# Revit family: HD148-2016.10.03-BT-STRIPSCREEN
name_source: partatom
category: Modelos genéricos
revit_build: Autodesk Revit 2017 (Build: 20160225_1515(x64)
units: mm (PartAtom-declared; Revit-internal decimal feet)

## family parameters
Compartido = No
Corte con vacíos al cargar = No
Cota de conector redondo = Diámetro de uso
Puede alojar armadura = No
Punto de cálculo de habitación = No
Se basa en plano de trabajo = No
Siempre vertical = Sí
Tipo de pieza = Normal

## types (1)
- Productos HD
    Alto THB = 1700 mm
    Ancho = 380 mm  [stored 1.24672 ft]
    BT_Alto = Aluzinc:12 mts, Acero corten: 15 mts
    BT_Ancho = 605 mm
    BT_Codigo_Origen = HD0148
    BT_Color = 100 colores a eleccion
    BT_Código_Línea = De Linea
    BT_Descripcion = Fleje de geometría plana Stripscreen con un ancho de 500mm y un largo
máximo de 5000 mm
    BT_EETT = Fleje de geometría plana con un ancho de 500mm y un largo
máximo de 5000 mm, fabricado en Aluzinc de espesor 1 mm.
El esquema de pintura considera la aplicación de un primer poliéster
de secado al horno por ambas caras, con un espesor de 5 ± 2
micras, y la aplicación de un esmalte de terminación poliéster
secado al horno por ambas caras, con un espesor total de 25 ± 2
micras (incluido el primer).
El sistema de instalación considera en su extremo inferior resortes
de acero inoxidable según cálculo y en su extremo superior
considera tensores de fierro galvanizado que permiten tensar el
fleje, los cuales se unen a éste mediante grilletes galvanizados
cuyas dimensiones se definirán de acuerdo a los requerimientos del
proyecto. Para evitar la ruptura del material en el tiempo, el fleje se
dobla en ambos extremos por sobre una barra de aluminio de 10
mm de diámetro y luego se prensa con 2 pletinas de aluminio de 50
mm de altura y 3mm de espesor que se fijarán mediante pernos y
tuercas.

que presentan una geometría transversal circular, con un diámetro de 

41 mm, los que son fabricados en aluzinc de espesor 0,5 mm.

El avance del panel es de 51 mm a eje.

El esquema de pintura considera la aplicación de un primer poliéster 

de secado al horno por ambas caras, con un espesor de 5 ±  2 micras, 

en color verde o gris y la aplicación de un esmalte de terminación 

poliéster secado al horno por una cara, con un espesor total de 25 ±  2 

micras (incluido el primer)

Se considera el uso de un perfil mullion ranurado, el que es fabricado 

en aluzinc de espesor 1,5 mm junto a otros accesorios propios de la 

solución definida, como la escuadra y traba.

Opciones de perforado estándar: #103 - Microperforados
    BT_Elemento = Celosías y Quiebravistas
    BT_Especialidad = Arquitectura
    BT_Fabricante = Hunter Douglas
    BT_Itemizado_Estandar_CDT = D 01 08 80
    BT_Marca = Hunter Douglas
    BT_MasterFormat® = 08 91 19
    BT_Material = Aluzinc 0.6-0.8-1.0mm, Acero corten: 0.6-1.0 mm
    BT_Nombre_Corto = Stripscreen
    BT_Nombre_Tecnico = Stripscreen
    BT_Peso = Aluzinc: 4.8-6.3-7.9 Kg/m2, Acero corten: 4.8-7.9 Kg/m2
    BT_Profundidad = Largo Máximo Aluzinc: 12 mts, Largo máximo Acero corten: 15 mts
    BT_SKU = 00 31 66
    BT_Uso = Exterior
    BT_Web_del_Producto = http://www.hunterdouglas.cl
    ID_Objeto = BT_F_F_770
    ID_Source = BIMTOOL
    Material = Metal

note: [stored X ft] marks values corroborated as IEEE doubles in the binary element streams (Revit-internal decimal feet)

## geometry (parser evidence)
native form markers: Sweep x14
no freeform markers — native parametric forms only
